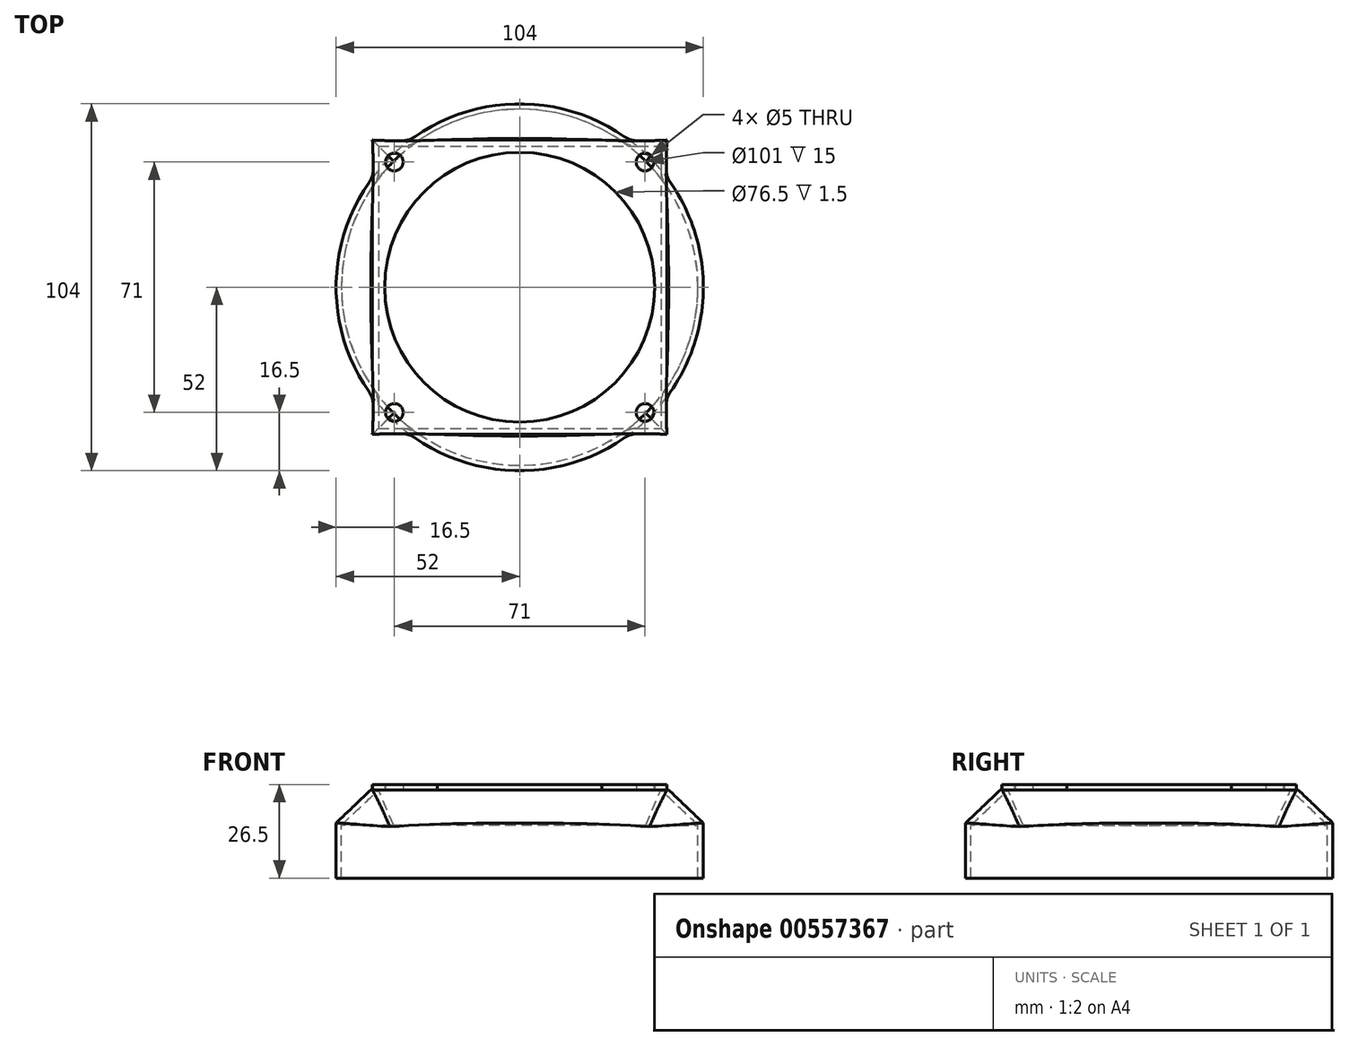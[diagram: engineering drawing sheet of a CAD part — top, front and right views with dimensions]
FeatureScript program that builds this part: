
annotation { "Feature Type Name" : "Feature", "Feature Type Description" : "" }
export const myFeature = defineFeature(function(context is Context, id is Id, definition is map)
    precondition{}
    {
        {
            var Q0;
            Q0=qCreatedBy(makeId("Top.planeOp"),FACE);
            var sketch = newSketch(context, id + "F0", { "sketchPlane" : qUnion([Q0])});
            skCircle(sketch, "E0", {"center": v(0, 0) * mm, "radius": 50.5 * mm});
            skSolve(sketch);
        }
        {
            var Q0;
            Q0=makeQuery(id+"F0.imprint","IMPRINT",FACE,{"disambiguationData":[TD([[makeQuery(id+"F0.imprint","IMPRINT",EDGE,{"derivedFrom":sQuery(id+"F0.wireOp",EDGE,"E0")}),1.0]])]});
            cPlane(context, id + "F1", {"entities" : qUnion([Q0]), "cplaneType" : CPlaneType.OFFSET, "offset" : 10 * mm, "width" : 150 * mm, "height" : 150 * mm});
        }
        {
            var Q0;
            Q0=qCreatedBy(id+"F1.planeOp",FACE);
            var sketch = newSketch(context, id + "F2", { "sketchPlane" : qUnion([Q0])});
            skLineSegment(sketch, "E1.bottom", {"start": v(-40, 40) * mm, "end": v(40, 40) * mm});
            skLineSegment(sketch, "E1.top", {"start": v(-40, -40) * mm, "end": v(40, -40) * mm});
            skLineSegment(sketch, "E1.left", {"start": v(-40, 40) * mm, "end": v(-40, -40) * mm});
            skLineSegment(sketch, "E1.right", {"start": v(40, 40) * mm, "end": v(40, -40) * mm});
            skPoint(sketch, "E1.middle", {"position": v(0, 0) * mm});
            skSolve(sketch);
        }
        {
            var Q0;
            Q0=makeQuery(id+"F0.imprint","IMPRINT",FACE,{"disambiguationData":[TD([[makeQuery(id+"F0.imprint","IMPRINT",EDGE,{"derivedFrom":sQuery(id+"F0.wireOp",EDGE,"E0")}),1.0]])]});
            var Q1;
            Q1=makeQuery(id+"F2.imprint","IMPRINT",FACE,{"disambiguationData":[TD([[makeQuery(id+"F2.imprint","IMPRINT",EDGE,{"derivedFrom":sQuery(id+"F2.wireOp",EDGE,"E1.bottom")}),-1.0]])]});
            var Q2;
            Q2=makeQuery(id+"F0.imprint","IMPRINT",FACE,{"disambiguationData":[TD([[makeQuery(id+"F0.imprint","IMPRINT",EDGE,{"derivedFrom":sQuery(id+"F0.wireOp",EDGE,"E0")}),1.0]])]});
            var Q3;
            Q3=makeQuery(id+"F2.imprint","IMPRINT",FACE,{"disambiguationData":[TD([[makeQuery(id+"F2.imprint","IMPRINT",EDGE,{"derivedFrom":sQuery(id+"F2.wireOp",EDGE,"E1.bottom")}),-1.0]])]});
            loft(context, id + "F3", {"sheetProfilesArray" : [{ "sheetProfileEntities" : qUnion([Q0]) }, { "sheetProfileEntities" : qUnion([Q1]) }], "wireProfilesArray" : [{ "wireProfileEntities" : qUnion([Q2]) }, { "wireProfileEntities" : qUnion([Q3]) }]});
        }
        {
            var Q0;
            Q0 = qSketchRegion(id + "F0", true);
            extrude(context, id + "F4", {"entities" : qUnion([Q0]), "operationType" : NewBodyOperationType.ADD, "oppositeDirection" : true, "depth" : 15 * mm, "offsetDistance" : 25 * mm});
        }
        {
            var Q0;
            Q0=makeQuery(id+"F4.opExtrude","CAP_FACE",FACE,{"disambiguationData":[OSD([sQuery(id+"F0.wireOp",EDGE,"E0")])],"isStart":false});
            var Q1;
            Q1=makeQuery(id+"F3.opLoft","CAP_FACE",FACE,{"disambiguationData":[OSD([makeQuery(id+"F2.imprint","IMPRINT",FACE,{"disambiguationData":[TD([[makeQuery(id+"F2.imprint","IMPRINT",EDGE,{"derivedFrom":sQuery(id+"F2.wireOp",EDGE,"E1.bottom")}),-1.0]])]})])],"isStart":true});
            shell(context, id + "F5", {"entities" : qUnion([Q0, Q1]), "thickness" : 1.5 * mm, "oppositeDirection" : true});
        }
        {
            var Q0;
            Q0=makeQuery(id+"F3.opLoft","CAP_FACE",FACE,{"disambiguationData":[OSD([makeQuery(id+"F2.imprint","IMPRINT",FACE,{"disambiguationData":[TD([[makeQuery(id+"F2.imprint","IMPRINT",EDGE,{"derivedFrom":sQuery(id+"F2.wireOp",EDGE,"E1.bottom")}),-1.0]])]})])],"isStart":true});
            var sketch = newSketch(context, id + "F6", { "sketchPlane" : qUnion([Q0])});
            skLineSegment(sketch, "E2.bottom", {"start": v(-40, 40) * mm, "end": v(40, 40) * mm});
            skLineSegment(sketch, "E2.top", {"start": v(-40, -40) * mm, "end": v(40, -40) * mm});
            skLineSegment(sketch, "E2.left", {"start": v(-40, 40) * mm, "end": v(-40, -40) * mm});
            skLineSegment(sketch, "E2.right", {"start": v(40, 40) * mm, "end": v(40, -40) * mm});
            skPoint(sketch, "E2.middle", {"position": v(0, 0) * mm});
            skCircle(sketch, "E3", {"center": v(-35.5, 35.5) * mm, "radius": 2.5 * mm});
            skLineSegment(sketch, "E4", {"start": v(0, 0) * mm, "end": v(0, 23.14) * mm, "construction": true});
            skLineSegment(sketch, "E5", {"start": v(0, 23.14) * mm, "end": v(0, 0) * mm, "construction": true});
            skLineSegment(sketch, "E6", {"start": v(26.08, 0) * mm, "end": v(0, 0) * mm, "construction": true});
            skCircle(sketch, "E7.MirrorC", {"center": v(35.5, 35.5) * mm, "radius": 2.5 * mm});
            skCircle(sketch, "E8.MirrorC", {"center": v(-35.5, -35.5) * mm, "radius": 2.5 * mm});
            skCircle(sketch, "E9.MirrorC", {"center": v(35.5, -35.5) * mm, "radius": 2.5 * mm});
            skCircle(sketch, "E10", {"center": v(0, 0) * mm, "radius": 38.25 * mm});
            skLineSegment(sketch, "E11.bottom", {"start": v(-41.7, 41.7) * mm, "end": v(41.7, 41.7) * mm});
            skLineSegment(sketch, "E11.top", {"start": v(-41.7, -41.7) * mm, "end": v(41.7, -41.7) * mm});
            skLineSegment(sketch, "E11.left", {"start": v(-41.7, 41.7) * mm, "end": v(-41.7, -41.7) * mm});
            skLineSegment(sketch, "E11.right", {"start": v(41.7, 41.7) * mm, "end": v(41.7, -41.7) * mm});
            skSolve(sketch);
        }
        {
            var Q0;
            Q0=makeQuery(id+"F6.imprint","IMPRINT",FACE,{"disambiguationData":[TD([[makeQuery(id+"F6.imprint","IMPRINT",EDGE,{"derivedFrom":sQuery(id+"F6.wireOp",EDGE,"E2.bottom")}),1.0]])]});
            var Q1;
            Q1=makeQuery(id+"F6.imprint","IMPRINT",FACE,{"disambiguationData":[TD([[makeQuery(id+"F6.imprint","IMPRINT",EDGE,{"derivedFrom":sQuery(id+"F6.wireOp",EDGE,"E2.bottom")}),-1.0]])]});
            extrude(context, id + "F7", {"entities" : qUnion([Q0, Q1]), "operationType" : NewBodyOperationType.ADD, "depth" : 1.5 * mm, "offsetDistance" : 25 * mm});
        }
    });
